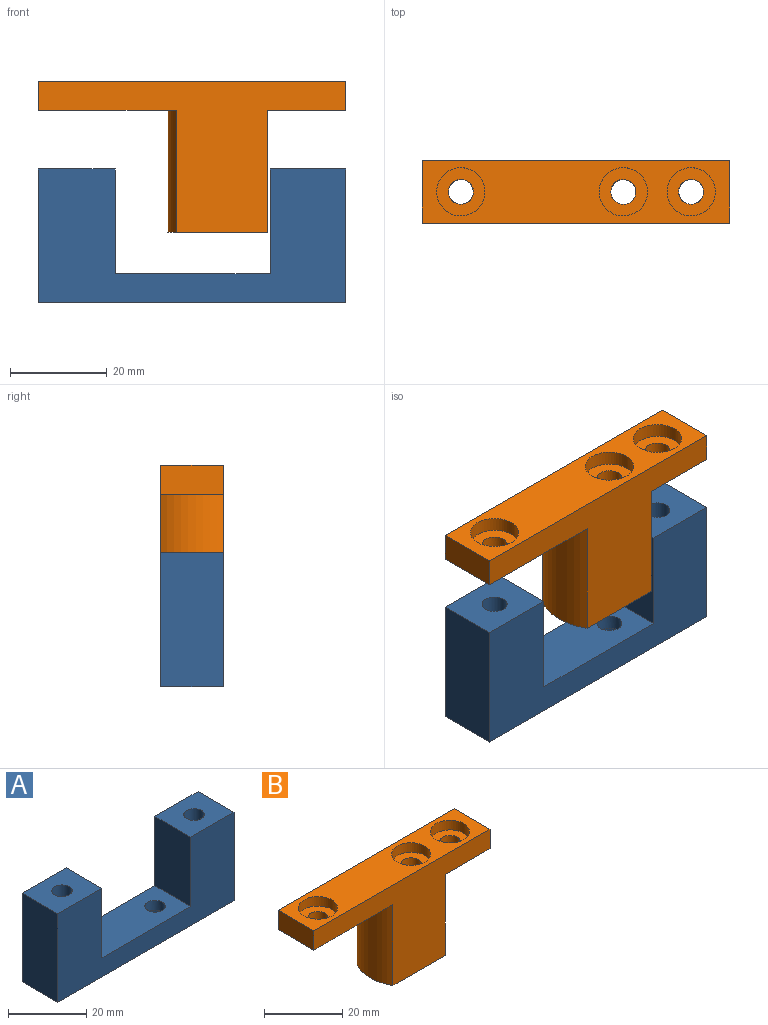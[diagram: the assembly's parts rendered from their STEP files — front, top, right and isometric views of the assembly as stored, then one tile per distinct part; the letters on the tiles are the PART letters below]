
ASSEMBLY  parts=2 mates=1
PART A: 19 faces, bbox 63.6x13x27.7 mm
  f0: plane 63.6x27.72mm, normal (0,-1,0), area 1067.1mm2, adj f1,f3,f7,f8,f15,f16,f17,f18
  f1: plane 27.72x13mm, normal (1,0,0), area 360.4mm2, adj f0,f2,f7,f17
  f2: plane 63.6x27.72mm, normal (0,1,0), area 1067.1mm2, adj f1,f3,f7,f8,f15,f16,f17,f18
  f3: plane 27.72x13mm, normal (-1,0,0), area 360.4mm2, adj f0,f2,f7,f16
  f4: cylinder r=2.6mm len=24.72mm, axis (0,0,1), area 403.1mm2, adj f14,f17
  f5: cylinder r=2.6mm len=24.72mm, axis (0,0,1), area 403.1mm2, adj f12,f16
  f6: cylinder r=2.6mm len=5.19mm, axis (0,0,-1), area 49.6mm2, adj f10,f15
  f7: plane 63.6x13mm, normal (0,0,-1), area 591.2mm2, adj f0,f1,f2,f3,f9,f11,f13
  f8: plane 21.68x13mm, normal (1,0,0), area 281.8mm2, adj f0,f2,f15,f16
  f9: cylinder r=5mm len=10mm, axis (0,0,-1), area 94.2mm2, adj f7,f10
  f10: plane 10x10mm, normal (0,0,-1), area 57.4mm2, adj f6,f9
  f11: cylinder r=5mm len=10mm, axis (0,0,-1), area 94.2mm2, adj f7,f12
  f12: plane 10x10mm, normal (0,0,-1), area 57.4mm2, adj f5,f11
  f13: cylinder r=5mm len=10mm, axis (0,0,-1), area 94.2mm2, adj f7,f14
  f14: plane 10x10mm, normal (0,0,-1), area 57.4mm2, adj f4,f13
  f15: plane 32.1x13mm, normal (0,0,1), area 396.1mm2, adj f0,f2,f6,f8,f18
  f16: plane 15.9x13mm, normal (0,0,1), area 185.5mm2, adj f0,f2,f3,f5,f8
  f17: plane 15.6x13mm, normal (0,0,1), area 181.6mm2, adj f0,f1,f2,f4,f18
  f18: plane 21.68x13mm, normal (-1,0,0), area 281.8mm2, adj f0,f2,f15,f17
PART B: 19 faces, bbox 63.6x13x31.3 mm
  f0: plane 63.6x31.34mm, normal (0,1,0), area 861.1mm2, adj f1,f6,f7,f8,f9,f10,f11,f18
  f1: plane 20.6x13mm, normal (0,0,-1), area 239.3mm2, adj f0,f4,f5,f11,f18
  f2: cylinder r=2.6mm len=5.19mm, axis (0,0,-1), area 49.6mm2, adj f10,f17
  f3: cylinder r=2.6mm len=5.19mm, axis (0,0,-1), area 49.6mm2, adj f9,f15
  f4: cylinder r=2.6mm len=28.34mm, axis (0,0,1), area 462.1mm2, adj f1,f13
  f5: plane 63.6x31.34mm, normal (0,-1,0), area 861.1mm2, adj f1,f6,f7,f8,f9,f10,f11,f18
  f6: plane 13x6.04mm, normal (1,0,0), area 78.5mm2, adj f0,f5,f8,f9
  f7: plane 13x6.04mm, normal (-1,0,0), area 78.5mm2, adj f0,f5,f8,f10
  f8: plane 63.6x13mm, normal (0,0,1), area 591.2mm2, adj f0,f5,f6,f7,f12,f14,f16
  f9: plane 16.2x13mm, normal (0,0,-1), area 189.4mm2, adj f0,f3,f5,f6,f18
  f10: plane 28.55x13mm, normal (0,0,-1), area 334.6mm2, adj f0,f2,f5,f7,f11
  f11: cylinder r=12.95mm len=25.3mm, axis (0,0,-1), area 344.6mm2, adj f0,f1,f5,f10
  f12: cylinder r=5mm len=10mm, axis (0,0,1), area 94.2mm2, adj f8,f13
  f13: plane 10x10mm, normal (0,0,1), area 57.4mm2, adj f4,f12
  f14: cylinder r=5mm len=10mm, axis (0,0,1), area 94.2mm2, adj f8,f15
  f15: plane 10x10mm, normal (0,0,1), area 57.4mm2, adj f3,f14
  f16: cylinder r=5mm len=10mm, axis (0,0,1), area 94.2mm2, adj f8,f17
  f17: plane 10x10mm, normal (0,0,1), area 57.4mm2, adj f2,f16
  f18: plane 25.3x13mm, normal (1,0,0), area 328.9mm2, adj f0,f1,f5,f9
PLACE A t=(17.4,-14.45,-56.51)mm
PLACE B t=(17.4,-14.45,-10.6)mm
MATE slider A.f4 <-> B.f3  axis (0,0,-1) through (9.45,-7.95,-53.51)mm
